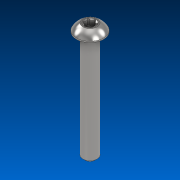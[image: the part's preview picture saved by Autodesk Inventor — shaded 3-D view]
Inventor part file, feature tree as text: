
AUTODESK INVENTOR PART (.ipt)
format: ipt  version: 2022.2 (Build 262287000, 287)  size: 166,912 bytes
history: native  units: in
note: dims shown in document units (in); Inventor stores cm internally (conversion verified against a paired STEP export)
features: direct_edit x1, chamfer x1, move_body x1
ambient origin geometry x8: Origin, YZ Plane, XZ Plane, XY Plane, X Axis, Y Axis, Z Axis, Center Point
bodies: Solid1 (feature_tree)
feature tree (3):
  direct_edit  "Direct Edit1"
  chamfer  "Chamfer2"  [1 undecoded]
  move_body  "Move1"
note: 1 required parameter value undecoded (feature->parameter linkage not recoverable at this tier; creation-order binding heuristic only, values carry confidence <= 0.55)
